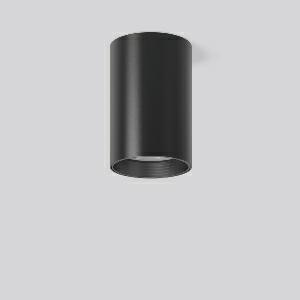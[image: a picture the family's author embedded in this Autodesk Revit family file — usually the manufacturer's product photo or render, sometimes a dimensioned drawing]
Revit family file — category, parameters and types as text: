
# Revit family: heledon_maxi_a_931222_003_3_37a5
name_source: partatom
category: Lighting Fixtures
units: mm (PartAtom-declared; Revit-internal decimal feet)

## family parameters
Cut with Voids When Loaded = No
Host = Face
Light Source = No
Part Type = Normal
Room Calculation Point = No
Round Connector Dimension = Use Diameter
Shared = No

## types (1)
- HELEDON maxi A (1 x LED Modul 935, 2850 lm, 3500)
    Apparent Load = 25 VA
    Approval mark = CE
    CIE Flux Codes = 96 100 100 100 100
    Color Rendering = 92
    Color Temperature = 3500
    Default Elevation = 1800 mm
    Description = Series: HELEDON maxi
Cylindrical surface-mounted downlight. Housing: die-cast aluminium, powder-coated. Internal ceiling frame polycarbonate with bayonet mounting. Black plastic ring and recessed LED to prevent glare from the side. Optical assembly with lens made of plastic (polycarbonate) for the best homogeneous light distribution - can be changed without tools. Best colour rendering index Ra>90. Suitable for Ceiling mounting. Easy installation with a separate ceiling frame with bayonet mounting and plug connection. Driver integrated. Connected via plug-in connector. High quality converter without flickering and stroboscopic effect. The following accessories can be mounted without use of tools: interchangeable lenses, decorative glasses, honeycomb louvre, clear and frosted diffusers, white interchangeable plastic ring. 
Colour: deep black, matt (RAL 9005)
Diameter: 123 mm
Height: 183 mm
Lamp: LED
Socket: without socket
Colour temperature: 3500K
Colour rendering index (CRI): 92
System power: 25 W
Rated luminous flux: 2850 lm
Luminous efficiency: 114 lm/W
Control gear: Regulated power supply
Protection class: I
Type of protection: IP 20
    Height = 183 mm
    Lamp = 1 x LED Modul 935
    Lamp Light Flux = 2850 lm
    Lamp count = 1
    Length = 123 mm
    Lifetime = 50000 h
    Luminous efficacy = 114 lm/W
    Manufacturer = RZB
    ModVariant = No
    Model = 931222.003.3
    Mounting Place = Ceiling
    Mounting Type = Surface mounted
    Number of Poles = 1
    OnlyDefault = Yes
    Power Factor = 1
    Product Name = HELEDON maxi A
    Product group = Surface mounted downlights
    ProductGroupID = 302
    Protection Class = Protection class I
    Protection Degree = IP 20
    RLX_Detail_Level = 1
    RLX_Emergency_Light_Flux = 0 lm
    RLX_Emergency_Type = 0
    RLX_Emergency_Type_DB = No
    RlxData = <blob elided: 97145 chars, md5=6e983c64>
    Socket = socket
    Standby Power = 0 W
    System Light Flux = 2850 lm
    System Power = 25 W
    Type Comments = Product without accessories
    Type Image = 931193.003.jpg
    URL = http://relux.com
    VarID = ---
    Voltage = 230 V
    Voltage Range = 220-240 V
    Weight = 0.00 kg
    Width = 0 mm  [stored 0 ft]

note: [stored X ft] marks values corroborated as IEEE doubles in the binary element streams (Revit-internal decimal feet)

## geometry (parser evidence)
native form markers: Blend x4, Sweep x12
no freeform markers — native parametric forms only
